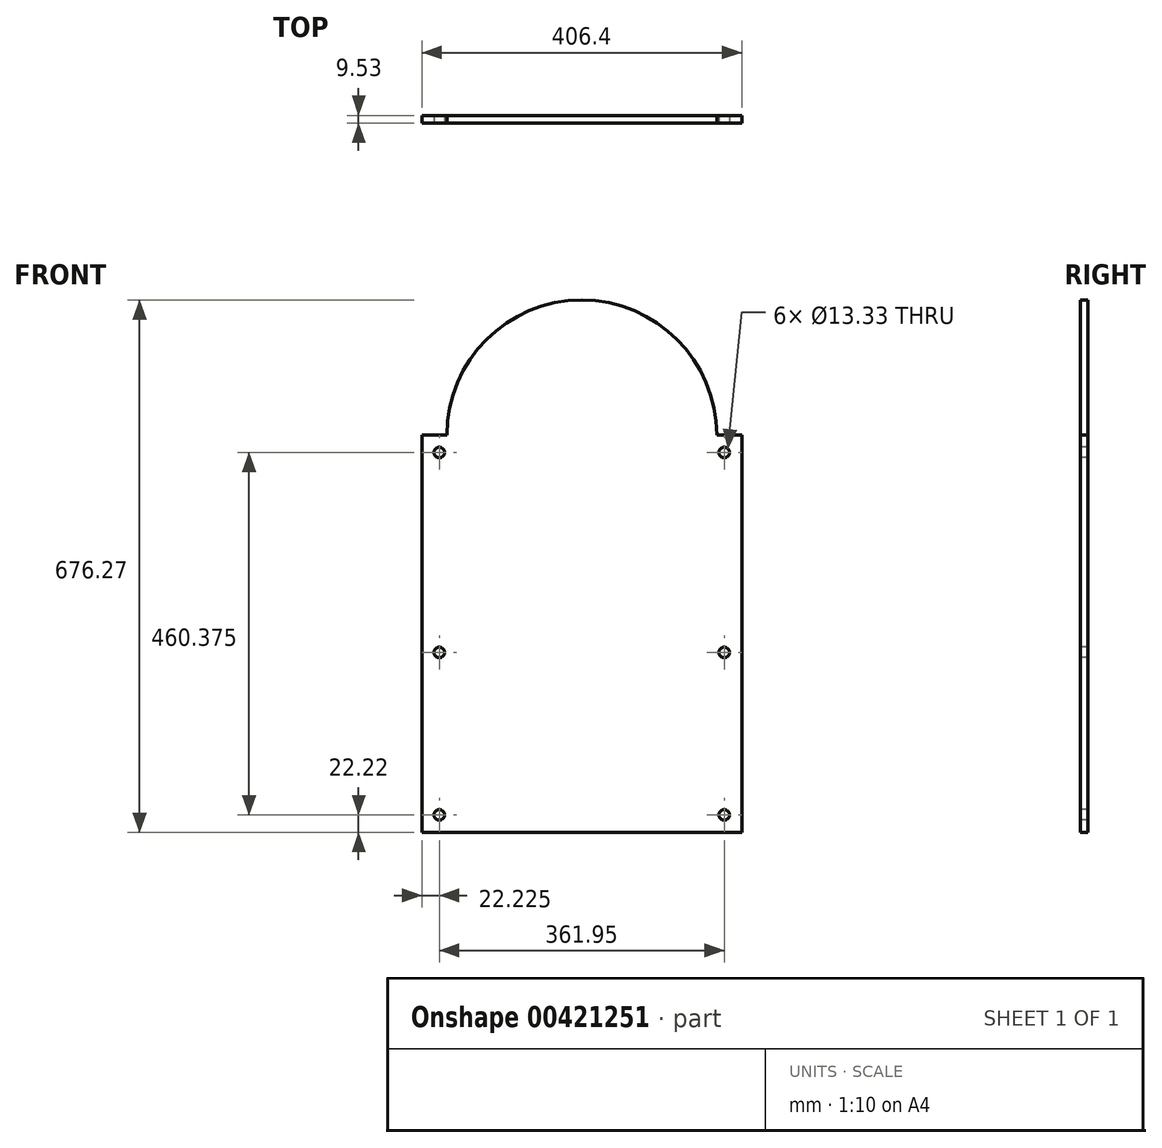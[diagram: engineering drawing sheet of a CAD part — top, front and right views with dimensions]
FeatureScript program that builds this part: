
annotation { "Feature Type Name" : "Feature", "Feature Type Description" : "" }
export const myFeature = defineFeature(function(context is Context, id is Id, definition is map)
    precondition{}
    {
        {
            var Q0;
            Q0=qCreatedBy(makeId("Front.planeOp"),FACE);
            var sketch = newSketch(context, id + "F0", { "sketchPlane" : qUnion([Q0])});
            skArc(sketch, "E0", {"start": v(171.45, 0) * mm, "mid": v(0, 171.45) * mm, "end": v(-171.45, 0) * mm});
            skLineSegment(sketch, "E1", {"start": v(-171.45, 0) * mm, "end": v(-203.2, 0) * mm});
            skLineSegment(sketch, "E2", {"start": v(-203.2, -504.83) * mm, "end": v(-203.2, 0) * mm});
            skLineSegment(sketch, "E3.MirrorCS", {"start": v(203.2, -504.83) * mm, "end": v(203.2, 0) * mm});
            skLineSegment(sketch, "E4", {"start": v(203.2, 0) * mm, "end": v(171.45, 0) * mm});
            skLineSegment(sketch, "E5", {"start": v(203.2, -504.83) * mm, "end": v(-203.2, -504.83) * mm});
            skSolve(sketch);
        }
        {
            var Q0;
            Q0 = qSketchRegion(id + "F0", true);
            extrude(context, id + "F1", {"entities" : qUnion([Q0]), "depth" : 9.52 * mm});
        }
        {
            var Q0;
            Q0=makeQuery(id+"F1.opExtrude","CAP_FACE",FACE,{"disambiguationData":[OSD([sQuery(id+"F0.wireOp",EDGE,"E0"),sQuery(id+"F0.wireOp",EDGE,"E1"),sQuery(id+"F0.wireOp",EDGE,"E2"),sQuery(id+"F0.wireOp",EDGE,"E3.MirrorCS"),sQuery(id+"F0.wireOp",EDGE,"E4"),sQuery(id+"F0.wireOp",EDGE,"E5")])],"isStart":false});
            var sketch = newSketch(context, id + "F2", { "sketchPlane" : qUnion([Q0])});
            skCircle(sketch, "E6", {"center": v(-180.98, -22.22) * mm, "radius": 6.67 * mm});
            skCircle(sketch, "E7.MirrorC", {"center": v(180.98, -22.22) * mm, "radius": 6.67 * mm});
            skCircle(sketch, "E8", {"center": v(180.98, -276.23) * mm, "radius": 6.67 * mm});
            skCircle(sketch, "E9.MirrorC", {"center": v(-180.98, -276.23) * mm, "radius": 6.67 * mm});
            skCircle(sketch, "E10", {"center": v(180.98, -482.6) * mm, "radius": 6.67 * mm});
            skCircle(sketch, "E11.MirrorC", {"center": v(-180.98, -482.6) * mm, "radius": 6.67 * mm});
            skSolve(sketch);
        }
        {
            var Q0;
            Q0 = qSketchRegion(id + "F2", true);
            extrude(context, id + "F3", {"entities" : qUnion([Q0]), "operationType" : NewBodyOperationType.REMOVE, "endBound" : BoundingType.THROUGH_ALL, "oppositeDirection" : true, "depth" : 25.4 * mm});
        }
    });
